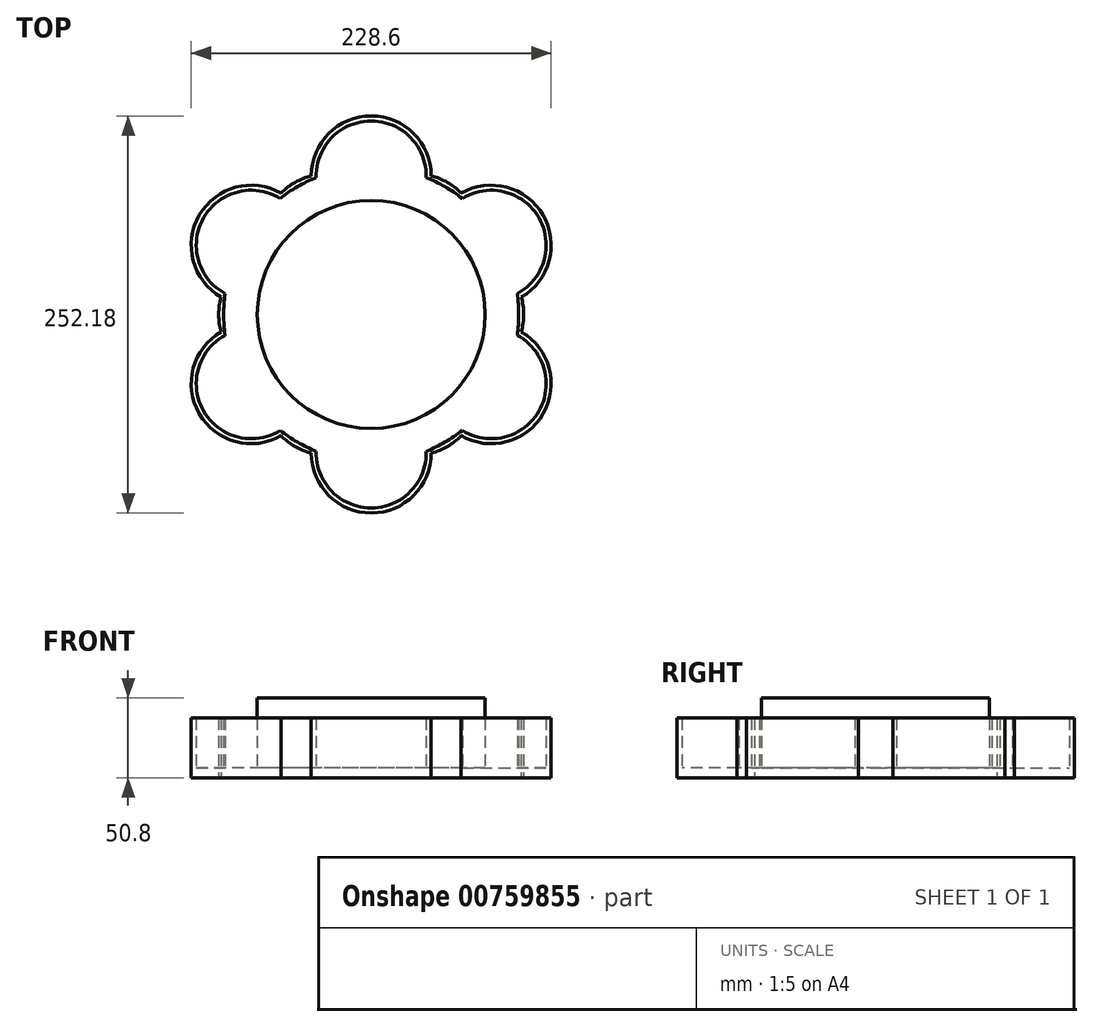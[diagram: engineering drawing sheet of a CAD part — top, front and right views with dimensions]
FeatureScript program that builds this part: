
annotation { "Feature Type Name" : "Feature", "Feature Type Description" : "" }
export const myFeature = defineFeature(function(context is Context, id is Id, definition is map)
    precondition{}
    {
        {
            var Q0;
            Q0=qCreatedBy(makeId("Top.planeOp"),FACE);
            var sketch = newSketch(context, id + "F0", { "sketchPlane" : qUnion([Q0])});
            skCircle(sketch, "E0.cCircle", {"center": v(0, 0) * mm, "radius": 101.6 * mm, "construction": true});
            skLineSegment(sketch, "E0.0", {"start": v(50.8, -87.99) * mm, "end": v(38.1, -87.99) * mm});
            skLineSegment(sketch, "E0.1", {"start": v(-50.8, -87.99) * mm, "end": v(-57.15, -76.99) * mm});
            skLineSegment(sketch, "E0.2", {"start": v(-101.6, 0) * mm, "end": v(-95.25, 11) * mm});
            skLineSegment(sketch, "E0.3", {"start": v(-50.8, 87.99) * mm, "end": v(-38.1, 87.99) * mm});
            skLineSegment(sketch, "E0.4", {"start": v(50.8, 87.99) * mm, "end": v(57.15, 76.99) * mm});
            skLineSegment(sketch, "E0.5", {"start": v(101.6, 0) * mm, "end": v(95.25, -11) * mm});
            skArc(sketch, "E1", {"start": v(38.1, 87.99) * mm, "mid": v(0, 126.09) * mm, "end": v(-38.1, 87.99) * mm});
            skArc(sketch, "E2", {"start": v(-57.15, 76.99) * mm, "mid": v(-109.2, 63.04) * mm, "end": v(-95.25, 11) * mm});
            skArc(sketch, "E3", {"start": v(-95.25, -11) * mm, "mid": v(-109.2, -63.04) * mm, "end": v(-57.15, -76.99) * mm});
            skArc(sketch, "E4", {"start": v(-38.1, -87.99) * mm, "mid": v(0, -126.09) * mm, "end": v(38.1, -87.99) * mm});
            skArc(sketch, "E5", {"start": v(57.15, -76.99) * mm, "mid": v(109.2, -63.04) * mm, "end": v(95.25, -11) * mm});
            skArc(sketch, "E6", {"start": v(95.25, 11) * mm, "mid": v(109.2, 63.04) * mm, "end": v(57.15, 76.99) * mm});
            skCircle(sketch, "E7", {"center": v(0, 0) * mm, "radius": 72.4 * mm});
            skLineSegment(sketch, "E8.trimOffspring", {"start": v(38.1, 87.99) * mm, "end": v(50.8, 87.99) * mm});
            skLineSegment(sketch, "E9.trimOffspring", {"start": v(57.15, -76.99) * mm, "end": v(50.8, -87.99) * mm});
            skLineSegment(sketch, "E10.trimOffspring", {"start": v(95.25, 11) * mm, "end": v(101.6, 0) * mm});
            skLineSegment(sketch, "E11.trimOffspring", {"start": v(-38.1, -87.99) * mm, "end": v(-50.8, -87.99) * mm});
            skLineSegment(sketch, "E12.trimOffspring", {"start": v(-95.25, -11) * mm, "end": v(-101.6, 0) * mm});
            skLineSegment(sketch, "E13.trimOffspring", {"start": v(-57.15, 76.99) * mm, "end": v(-50.8, 87.99) * mm});
            skSolve(sketch);
        }
        {
            var Q0;
            Q0=makeQuery(id+"F0.imprint","IMPRINT",FACE,{"disambiguationData":[TD([[makeQuery(id+"F0.imprint","IMPRINT",EDGE,{"derivedFrom":sQuery(id+"F0.wireOp",EDGE,"E0.0")}),-1.0]])]});
            extrude(context, id + "F1", {"entities" : qUnion([Q0]), "depth" : 6.35 * mm, "offsetDistance" : 25.4 * mm});
        }
        {
            var Q0;
            Q0=makeQuery(id+"F0.imprint","IMPRINT",FACE,{"disambiguationData":[TD([[makeQuery(id+"F0.imprint","IMPRINT",EDGE,{"derivedFrom":sQuery(id+"F0.wireOp",EDGE,"E7")}),1.0]])]});
            extrude(context, id + "F2", {"entities" : qUnion([Q0]), "operationType" : NewBodyOperationType.ADD, "depth" : 50.8 * mm, "offsetDistance" : 25.4 * mm});
        }
        {
            var Q0;
            Q0=makeQuery(id+"F1.opExtrude","SWEPT_EDGE",EDGE,{"disambiguationData":[OSD([sQuery(id+"F0.wireOp",EDGE,"E0.4"),sQuery(id+"F0.wireOp",EDGE,"E8.trimOffspring")])]});
            var Q1;
            Q1=makeQuery(id+"F1.opExtrude","SWEPT_EDGE",EDGE,{"disambiguationData":[OSD([sQuery(id+"F0.wireOp",EDGE,"E0.5"),sQuery(id+"F0.wireOp",EDGE,"E10.trimOffspring")])]});
            var Q2;
            Q2=makeQuery(id+"F1.opExtrude","SWEPT_EDGE",EDGE,{"disambiguationData":[OSD([sQuery(id+"F0.wireOp",EDGE,"E0.0"),sQuery(id+"F0.wireOp",EDGE,"E9.trimOffspring")])]});
            var Q3;
            Q3=makeQuery(id+"F1.opExtrude","SWEPT_EDGE",EDGE,{"disambiguationData":[OSD([sQuery(id+"F0.wireOp",EDGE,"E0.1"),sQuery(id+"F0.wireOp",EDGE,"E11.trimOffspring")])]});
            var Q4;
            Q4=makeQuery(id+"F1.opExtrude","SWEPT_EDGE",EDGE,{"disambiguationData":[OSD([sQuery(id+"F0.wireOp",EDGE,"E0.2"),sQuery(id+"F0.wireOp",EDGE,"E12.trimOffspring")])]});
            var Q5;
            Q5=makeQuery(id+"F1.opExtrude","SWEPT_EDGE",EDGE,{"disambiguationData":[OSD([sQuery(id+"F0.wireOp",EDGE,"E0.3"),sQuery(id+"F0.wireOp",EDGE,"E13.trimOffspring")])]});
            fillet(context, id + "F3", {"entities" : qUnion([Q0, Q1, Q2, Q3, Q4, Q5]), "radius" : 38.1 * mm, "tangentPropagation" : true, "allowEdgeOverflow" : false});
        }
        {
            var Q0;
            Q0=makeQuery(id+"F1.opExtrude","CAP_FACE",FACE,{"disambiguationData":[OSD([sQuery(id+"F0.wireOp",EDGE,"E0.0"),sQuery(id+"F0.wireOp",EDGE,"E0.1"),sQuery(id+"F0.wireOp",EDGE,"E0.2"),sQuery(id+"F0.wireOp",EDGE,"E0.3"),sQuery(id+"F0.wireOp",EDGE,"E0.4"),sQuery(id+"F0.wireOp",EDGE,"E0.5"),sQuery(id+"F0.wireOp",EDGE,"E1"),sQuery(id+"F0.wireOp",EDGE,"E2"),sQuery(id+"F0.wireOp",EDGE,"E3"),sQuery(id+"F0.wireOp",EDGE,"E4"),sQuery(id+"F0.wireOp",EDGE,"E5"),sQuery(id+"F0.wireOp",EDGE,"E6"),sQuery(id+"F0.wireOp",EDGE,"E7"),sQuery(id+"F0.wireOp",EDGE,"E8.trimOffspring"),sQuery(id+"F0.wireOp",EDGE,"E9.trimOffspring"),sQuery(id+"F0.wireOp",EDGE,"E10.trimOffspring"),sQuery(id+"F0.wireOp",EDGE,"E11.trimOffspring"),sQuery(id+"F0.wireOp",EDGE,"E12.trimOffspring"),sQuery(id+"F0.wireOp",EDGE,"E13.trimOffspring")])],"isStart":false});
            var sketch = newSketch(context, id + "F4", { "sketchPlane" : qUnion([Q0])});
            skArc(sketch, "E14", {"start": v(-57.85, 73.7) * mm, "mid": v(-106.45, 61.46) * mm, "end": v(-92.76, 13.24) * mm});
            skArc(sketch, "E15", {"start": v(34.9, 86.95) * mm, "mid": v(0, 122.91) * mm, "end": v(-34.9, 86.95) * mm});
            skArc(sketch, "E16", {"start": v(92.76, 13.24) * mm, "mid": v(106.45, 61.46) * mm, "end": v(57.85, 73.7) * mm});
            skArc(sketch, "E17", {"start": v(57.85, -73.7) * mm, "mid": v(106.45, -61.46) * mm, "end": v(92.76, -13.24) * mm});
            skArc(sketch, "E18", {"start": v(-34.9, -86.95) * mm, "mid": v(0, -122.91) * mm, "end": v(34.9, -86.95) * mm});
            skArc(sketch, "E19", {"start": v(-92.76, -13.24) * mm, "mid": v(-106.45, -61.46) * mm, "end": v(-57.85, -73.7) * mm});
            skArc(sketch, "E20", {"start": v(-92.76, 13.24) * mm, "mid": v(-93.7, 0) * mm, "end": v(-92.76, -13.24) * mm});
            skArc(sketch, "E21.trimOffspring", {"start": v(-34.9, 86.95) * mm, "mid": v(-46.85, 81.14) * mm, "end": v(-57.85, 73.7) * mm});
            skArc(sketch, "E22.trimOffspring", {"start": v(57.85, 73.7) * mm, "mid": v(46.85, 81.14) * mm, "end": v(34.9, 86.95) * mm});
            skArc(sketch, "E23.trimOffspring", {"start": v(92.76, -13.24) * mm, "mid": v(93.7, 0) * mm, "end": v(92.76, 13.24) * mm});
            skArc(sketch, "E24.trimOffspring", {"start": v(34.9, -86.95) * mm, "mid": v(46.85, -81.14) * mm, "end": v(57.85, -73.7) * mm});
            skArc(sketch, "E25.trimOffspring", {"start": v(-57.85, -73.7) * mm, "mid": v(-46.85, -81.14) * mm, "end": v(-34.9, -86.95) * mm});
            skSolve(sketch);
        }
        {
            var Q0;
            Q0=makeQuery(id+"F4.imprint","IMPRINT",FACE,{"disambiguationData":[TD([[makeQuery(id+"F4.imprint","IMPRINT",EDGE,{"derivedFrom":sQuery(id+"F4.wireOp",EDGE,"E14")}),-1.0]])]});
            extrude(context, id + "F5", {"entities" : qUnion([Q0]), "operationType" : NewBodyOperationType.ADD, "depth" : 31.75 * mm, "offsetDistance" : 25.4 * mm});
        }
    });
